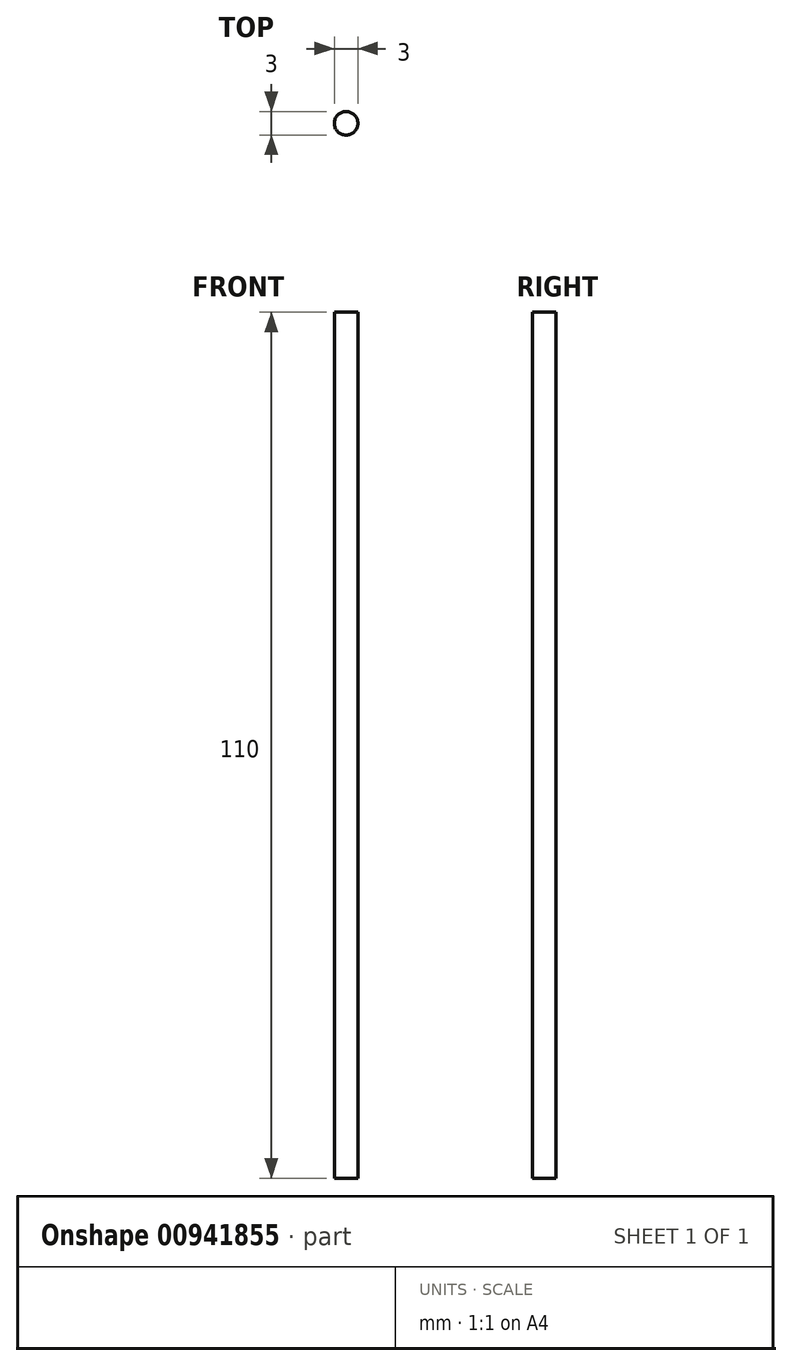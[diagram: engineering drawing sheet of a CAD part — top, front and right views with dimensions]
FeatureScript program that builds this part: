
annotation { "Feature Type Name" : "Feature", "Feature Type Description" : "" }
export const myFeature = defineFeature(function(context is Context, id is Id, definition is map)
    precondition{}
    {
        {
            var Q0;
            Q0=qCreatedBy(makeId("Top.planeOp"),FACE);
            var sketch = newSketch(context, id + "F0", { "sketchPlane" : qUnion([Q0])});
            skCircle(sketch, "E0", {"center": v(0, 0) * mm, "radius": 1.5 * mm});
            skSolve(sketch);
        }
        {
            var Q0;
            Q0 = qSketchRegion(id + "F0", true);
            extrude(context, id + "F1", {"entities" : qUnion([Q0]), "depth" : 55 * mm, "offsetDistance" : 25.4 * mm, "hasSecondDirection" : true, "secondDirectionOppositeDirection" : true, "secondDirectionDepth" : 55 * mm});
        }
    });
